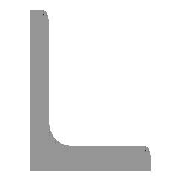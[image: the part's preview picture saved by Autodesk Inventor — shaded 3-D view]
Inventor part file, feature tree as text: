
AUTODESK INVENTOR PART (.ipt)
format: ipt  version: 2016 (Build 200138000, 138)  size: 126,976 bytes
history: native  units: mm (DEFAULTED — no unit token found)
features: other x4, sketch x3, plane x2, extrude x1
ambient origin geometry x8: Origin, YZ Plane, XZ Plane, XY Plane, X Axis, Y Axis, Z Axis, Center Point
bodies: Solid1 (feature_tree)
feature tree (10):
  parser-record x1  (decoder bookkeeping rows leaked as tree rows — omitted from the tree; the rows remain in map.json)
  other  "Driven Length"
  other  "Plano inicial"
  other  "Plano final"
  extrude  "Cuerpo"  Depth=38.1mm
  sketch  "Boceto5"  dims[d3=4.7625mm d4=2400.0mm d5=0.0mm d10=0.0mm d11=0.0mm d12=-0.0mm d13=2400.0mm d14=4.826mm d15=2.286mm d16=90.0deg d17=2400.0mm]
  plane  "Plano de trabajo4"
  sketch  "Sketch3"  dims[d0=38.1mm d1=38.1mm]
  plane  "Work Plane3"
  sketch  "Sketch4"  dims[d2=4.7625mm]
